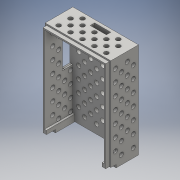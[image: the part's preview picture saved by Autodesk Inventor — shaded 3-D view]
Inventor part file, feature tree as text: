
AUTODESK INVENTOR PART (.ipt)
format: ipt  version: 2016 (Build 200138000, 138)  size: 646,656 bytes
history: native  units: mm
features: sketch x18, extrude x13, hole x2
ambient origin geometry x8: Origin, YZ Plane, XZ Plane, XY Plane, X Axis, Y Axis, Z Axis, Center Point
bodies: Solid1 (feature_tree)
feature tree (33):
  extrude  "Extrusion1"  Depth=60.0mm
  extrude  "Extrusion3"  Depth=6.0mm
  extrude  "Extrusion5"  Depth=90.0mm
  extrude  "Extrusion7"  Depth=27.0mm
  sketch  "Sketch9"  dims[d13=4.3mm d17=15.0mm]
  sketch  "Sketch10"  dims[d18=27.0mm d19=45.0mm]
  extrude  "Extrusion8"  Depth=15.0mm
  extrude  "Extrusion9"  Depth=45.0mm
  extrude  "Extrusion10"  Depth=90.0mm
  sketch  "Sketch14"  dims[d33=1.5mm d34=0.0mm d40=63.0mm]
  sketch  "Sketch16"  dims[d41=1.5mm d42=30.0mm d43=0.0mm]
  hole  "Hole3"  [1 undecoded]
  hole  "Hole4"  [1 undecoded]
  extrude  "Extrusion12"  Depth=63.0mm
  extrude  "Extrusion13"  Depth=1.5mm TaperAngle=0.0deg
  sketch  "Sketch19"  dims[d50=3.0mm d51=3.0mm]
  extrude  "Extrusion14"  Depth=4.3mm
  sketch  "Sketch21"  dims[d62=3.8mm]
  extrude  "Extrusion16"  Depth=3.0mm
  extrude  "Extrusion17"  Depth=3.0mm
  extrude  "Extrusion18"  Depth=3.0mm
  sketch  "Sketch1"  dims[d0=60.0mm d1=4.3mm]
  sketch  "Sketch3"  dims[d2=6.0mm d3=6.0mm]
  sketch  "Sketch5"  dims[d6=90.0mm d7=4.3mm]
  sketch  "Sketch8"  dims[d10=15.0mm d12=27.0mm]
  sketch  "Sketch11"  dims[d20=1.5mm d21=0.0mm d25=90.0mm]
  sketch  "Sketch12"  dims[d26=30.0mm d27=1.5mm d28=0.0mm]
  sketch  "Sketch13"  dims[d31=90.0mm d32=30.0mm]
  sketch  "Sketch17"  dims[d46=7.5mm d47=4.3mm]
  sketch  "Sketch18"  dims[d48=6.0mm d49=3.0mm]
  sketch  "Sketch20"  dims[d52=3.0mm d53=3.0mm]
  sketch  "Sketch22"  dims[d63=7.5mm]
  sketch  "Sketch23"  dims[d64=4.3mm d65=6.0mm d66=4.3mm d67=6.0mm d69=3.0mm d70=3.0mm d71=3.0mm d72=3.0mm d80=30.0mm d81=0.0mm d82=3.7mm d83=2.0mm d84=0.0mm d85=3.7mm d86=2.0mm d87=0.0mm d99=4.35mm d100=6.0mm d101=4.0mm d102=2.0mm d103=90.0deg d104=8.0mm d105=20.594885mm d106=4.35mm d107=6.0mm d108=4.0mm d109=2.0mm d110=90.0deg d111=8.0mm d112=20.594885mm d114=10.0mm d115=0.0mm d116=3.65mm d117=4.35mm d118=4.35mm d119=4.35mm d120=4.35mm d121=4.35mm d122=4.35mm d123=4.35mm d124=4.35mm d125=4.35mm d126=4.35mm d127=1.5mm d128=0.0mm d129=4.35mm d130=4.35mm d131=1.5mm d132=0.0mm d135=1.5mm d136=0.0mm d137=9.0mm d138=3.0mm d139=0.0mm d140=1.5mm d141=0.0mm]
note: 2 required parameter values undecoded (feature->parameter linkage not recoverable at this tier; creation-order binding heuristic only, values carry confidence <= 0.55)
